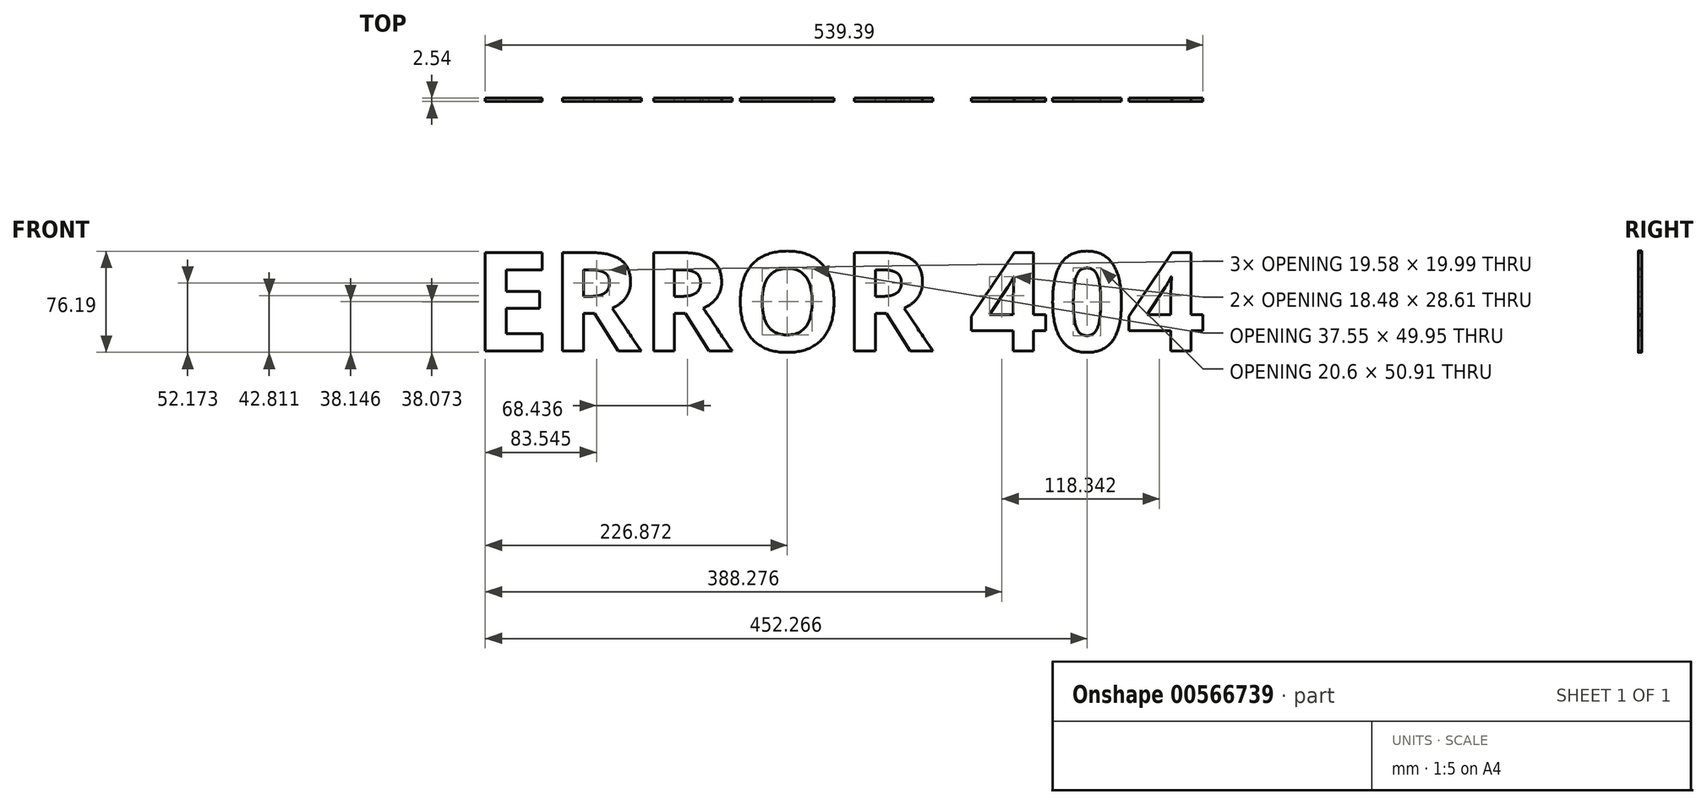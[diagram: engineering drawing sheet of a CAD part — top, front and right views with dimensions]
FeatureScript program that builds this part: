
annotation { "Feature Type Name" : "Feature", "Feature Type Description" : "" }
export const myFeature = defineFeature(function(context is Context, id is Id, definition is map)
    precondition{}
    {
        {
            var Q0;
            Q0=qCreatedBy(makeId("Front.planeOp"),FACE);
            var sketch = newSketch(context, id + "F0", { "sketchPlane" : qUnion([Q0])});
            skText(sketch, "E0", { "text": "ERROR 404", "fontName": "OpenSans-Bold.ttf"});
            skLineSegment(sketch, "E1", {"start": v(0, 37.32) * mm, "end": v(0, -37.32) * mm});
            skPoint(sketch, "E2", {"position": v(0, 0) * mm});
            const initialGuessF0  = {"E0": [-0.2777, -0.03732, 1, 0, 0.07464]};
            skSetInitialGuess(sketch, initialGuessF0);
            skSolve(sketch);
        }
        {
            var Q0;
            Q0 = qSketchRegion(id + "F0", true);
            extrude(context, id + "F1", {"entities" : qUnion([Q0]), "depth" : 2.54 * mm, "offsetDistance" : 25.4 * mm});
        }
    });
